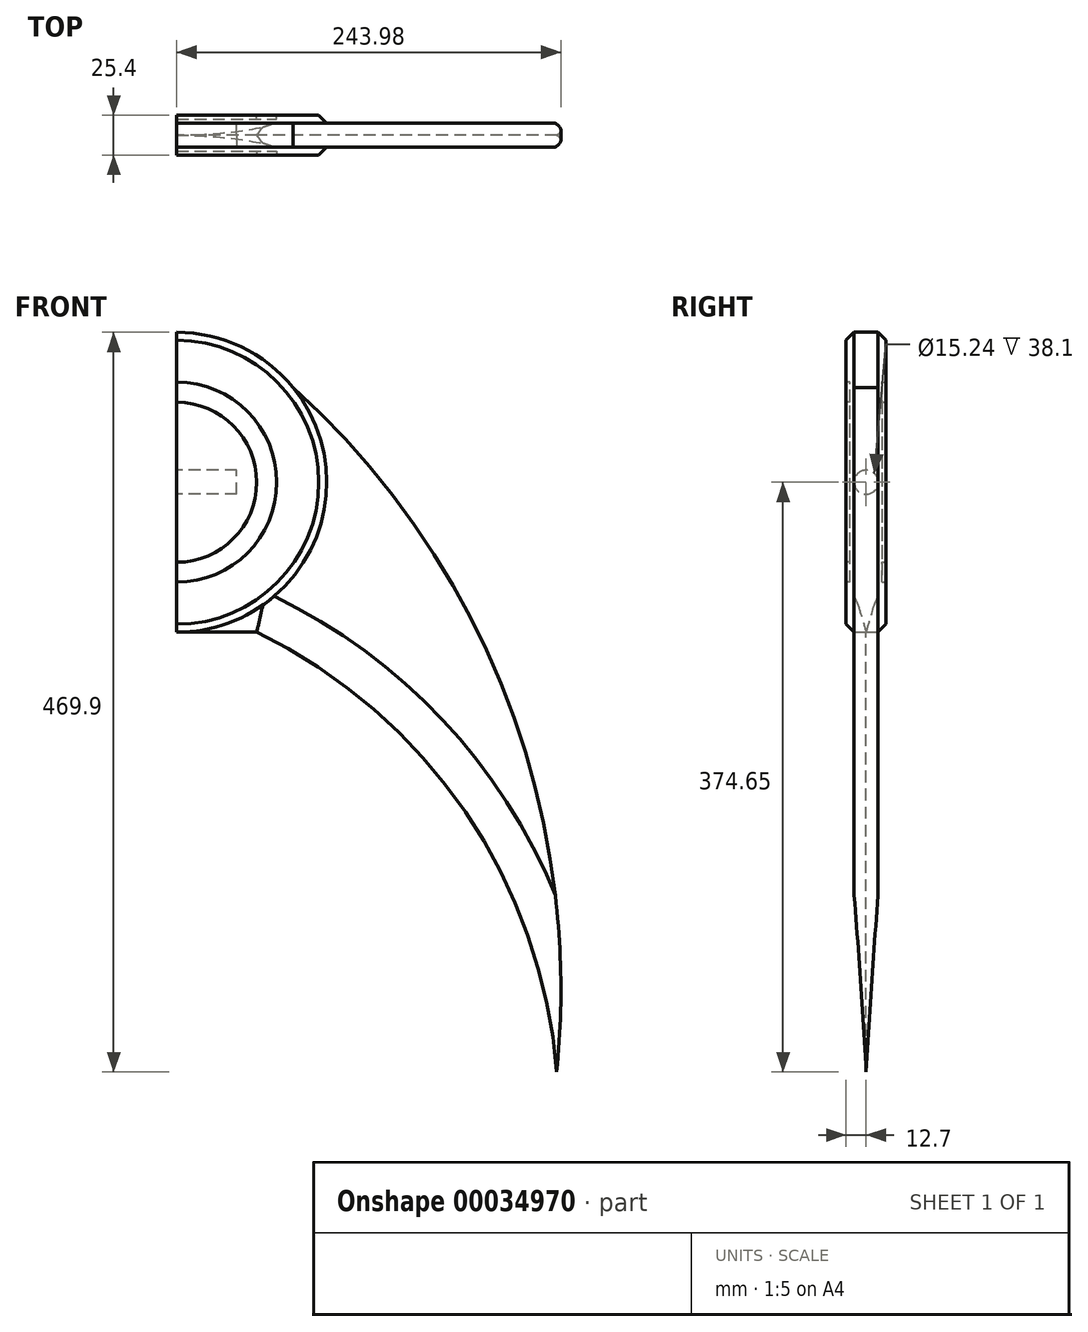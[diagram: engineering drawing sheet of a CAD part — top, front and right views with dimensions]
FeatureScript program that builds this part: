
annotation { "Feature Type Name" : "Feature", "Feature Type Description" : "" }
export const myFeature = defineFeature(function(context is Context, id is Id, definition is map)
    precondition{}
    {
        {
            var Q0;
            Q0=qCreatedBy(makeId("Right.planeOp"),FACE);
            var sketch = newSketch(context, id + "F0", { "sketchPlane" : qUnion([Q0])});
            skCircle(sketch, "E0", {"center": v(0, 0) * mm, "radius": 7.62 * mm});
            skSolve(sketch);
        }
        {
            var Q0;
            Q0=makeQuery(id+"F0.imprint","IMPRINT",FACE,{"disambiguationData":[TD([[makeQuery(id+"F0.imprint","IMPRINT",EDGE,{"derivedFrom":sQuery(id+"F0.wireOp",EDGE,"E0")}),1.0]])]});
            extrude(context, id + "F1", {"entities" : qUnion([Q0]), "depth" : 38.1 * mm});
        }
        {
            var Q0;
            Q0=qCreatedBy(makeId("Front.planeOp"),FACE);
            var sketch = newSketch(context, id + "F2", { "sketchPlane" : qUnion([Q0])});
            skLineSegment(sketch, "E1.0", {"start": v(38.1, 7.62) * mm, "end": v(38.1, -7.62) * mm});
            skArc(sketch, "E2", {"start": v(111.98, 60.11) * mm, "mid": v(79, 86.02) * mm, "end": v(38.1, 95.25) * mm});
            skLineSegment(sketch, "E3", {"start": v(38.1, 0) * mm, "end": v(38.1, 95.25) * mm});
            skLineSegment(sketch, "E4", {"start": v(38.1, 0) * mm, "end": v(38.1, -95.25) * mm});
            skLineSegment(sketch, "E5", {"start": v(38.1, -95.25) * mm, "end": v(88.9, -95.25) * mm});
            skArc(sketch, "E6", {"start": v(279.4, -374.65) * mm, "mid": v(221.44, -209.52) * mm, "end": v(88.9, -95.25) * mm});
            skArc(sketch, "E7", {"start": v(279.4, -374.65) * mm, "mid": v(247.68, -137.25) * mm, "end": v(111.98, 60.11) * mm});
            skSolve(sketch);
        }
        {
            var Q0;
            {var subQ3=sQuery(id+"F2.wireOp",EDGE,"E2");Q0=makeQuery(id+"F2.imprint","IMPRINT",FACE,{"disambiguationData":[TD([[makeQuery(id+"F2.imprint","IMPRINT",EDGE,{"derivedFrom":subQ3}),1.0]])]});}
            extrude(context, id + "F3", {"entities" : qUnion([Q0]), "operationType" : NewBodyOperationType.ADD, "endBound" : BoundingType.SYMMETRIC, "depth" : 15.24 * mm});
        }
        {
            var Q0;
            Q0=makeQuery(id+"F3.opExtrude","CAP_EDGE",EDGE,{"disambiguationData":[OSD([sQuery(id+"F2.wireOp",EDGE,"E6")])],"isStart":false});
            var Q1;
            Q1=makeQuery(id+"F3.opExtrude","CAP_EDGE",EDGE,{"disambiguationData":[OSD([sQuery(id+"F2.wireOp",EDGE,"E5")])],"isStart":false});
            chamfer(context, id + "F4", {"entities" : qUnion([Q0, Q1]), "chamferType" : ChamferType.TWO_OFFSETS, "width1" : 7.62 * mm, "oppositeDirection" : false, "width2" : 25.4 * mm, "tangentPropagation" : true});
        }
        {
            var Q0;
            Q0=makeQuery(id+"F3.opExtrude","CAP_EDGE",EDGE,{"disambiguationData":[OSD([sQuery(id+"F2.wireOp",EDGE,"E6")])],"isStart":true});
            var Q1;
            Q1=makeQuery(id+"F3.opExtrude","CAP_EDGE",EDGE,{"disambiguationData":[OSD([sQuery(id+"F2.wireOp",EDGE,"E5")])],"isStart":true});
            chamfer(context, id + "F5", {"entities" : qUnion([Q0, Q1]), "chamferType" : ChamferType.TWO_OFFSETS, "width1" : 25.4 * mm, "oppositeDirection" : false, "width2" : 7.62 * mm, "tangentPropagation" : true});
        }
        {
            var Q0;
            Q0=qCreatedBy(makeId("Front.planeOp"),FACE);
            var sketch = newSketch(context, id + "F6", { "sketchPlane" : qUnion([Q0])});
            skLineSegment(sketch, "E8.0", {"start": v(38.1, 0) * mm, "end": v(38.1, 95.25) * mm});
            skCircle(sketch, "E9", {"center": v(38.1, 0) * mm, "radius": 95.25 * mm});
            skLineSegment(sketch, "E10", {"start": v(38.1, 0) * mm, "end": v(38.1, -95.25) * mm});
            skSolve(sketch);
        }
        {
            var Q0;
            {var subQ2=sQuery(id+"F6.wireOp",EDGE,"E8.0");Q0=makeQuery(id+"F6.imprint","IMPRINT",FACE,{"disambiguationData":[TD([[makeQuery(id+"F6.imprint","IMPRINT",EDGE,{"derivedFrom":subQ2}),-1.0]])]});}
            extrude(context, id + "F7", {"entities" : qUnion([Q0]), "operationType" : NewBodyOperationType.ADD, "endBound" : BoundingType.SYMMETRIC, "depth" : 25.4 * mm});
        }
        {
            var Q0;
            Q0=makeQuery(id+"F7.opExtrude","CAP_EDGE",EDGE,{"disambiguationData":[OSD([sQuery(id+"F6.wireOp",EDGE,"E9")])],"isStart":false});
            var Q1;
            Q1=makeQuery(id+"F7.opExtrude","CAP_EDGE",EDGE,{"disambiguationData":[OSD([sQuery(id+"F6.wireOp",EDGE,"E9")])],"isStart":true});
            chamfer(context, id + "F8", {"entities" : qUnion([Q0, Q1]), "width" : 5.08 * mm, "tangentPropagation" : true});
        }
        {
            var Q0;
            Q0=makeQuery(id+"F7.opExtrude","CAP_FACE",FACE,{"disambiguationData":[OSD([sQuery(id+"F6.wireOp",EDGE,"E8.0"),sQuery(id+"F6.wireOp",EDGE,"E9"),sQuery(id+"F6.wireOp",EDGE,"E10")])],"isStart":false});
            var sketch = newSketch(context, id + "F9", { "sketchPlane" : qUnion([Q0])});
            skCircle(sketch, "E11", {"center": v(38.1, 0) * mm, "radius": 63.5 * mm});
            skCircle(sketch, "E12", {"center": v(38.1, 0) * mm, "radius": 50.8 * mm});
            skSolve(sketch);
        }
        {
            var Q0;
            {var subQ0=makeQuery(id+"F7.opExtrude","CAP_EDGE",EDGE,{"disambiguationData":[OSD([sQuery(id+"F6.wireOp",EDGE,"E8.0"),sQuery(id+"F6.wireOp",EDGE,"E10")])],"isStart":false});var subQ3=sQuery(id+"F9.wireOp",EDGE,"E11");var subQ6=makeQuery(id+"F9.imprint","INTERSECT",VERTEX,{"disambiguationData":[OD(0.0)],"derivedFrom":[subQ0,subQ3]});Q0=makeQuery(id+"F9.imprint","IMPRINT",FACE,{"disambiguationData":[TD([[makeQuery(id+"F9.imprint","IMPRINT",EDGE,{"disambiguationData":[TD([[subQ6,1.0]])],"derivedFrom":subQ3}),1.0]])]});}
            extrude(context, id + "F10", {"entities" : qUnion([Q0]), "operationType" : NewBodyOperationType.REMOVE, "oppositeDirection" : true, "depth" : 2.54 * mm});
        }
        {
            var Q0;
            Q0=makeQuery(id+"F7.opExtrude","CAP_FACE",FACE,{"disambiguationData":[OSD([sQuery(id+"F6.wireOp",EDGE,"E8.0"),sQuery(id+"F6.wireOp",EDGE,"E9"),sQuery(id+"F6.wireOp",EDGE,"E10")])],"isStart":true});
            var sketch = newSketch(context, id + "F11", { "sketchPlane" : qUnion([Q0])});
            skCircle(sketch, "E13", {"center": v(-38.1, 0) * mm, "radius": 63.5 * mm});
            skCircle(sketch, "E14", {"center": v(-38.1, 0) * mm, "radius": 50.8 * mm});
            skSolve(sketch);
        }
        {
            var Q0;
            {var subQ0=makeQuery(id+"F7.opExtrude","CAP_EDGE",EDGE,{"disambiguationData":[OSD([sQuery(id+"F6.wireOp",EDGE,"E8.0"),sQuery(id+"F6.wireOp",EDGE,"E10")])],"isStart":true});var subQ3=sQuery(id+"F11.wireOp",EDGE,"E13");var subQ6=makeQuery(id+"F11.imprint","INTERSECT",VERTEX,{"disambiguationData":[OD(0.0)],"derivedFrom":[subQ0,subQ3]});Q0=makeQuery(id+"F11.imprint","IMPRINT",FACE,{"disambiguationData":[TD([[makeQuery(id+"F11.imprint","IMPRINT",EDGE,{"disambiguationData":[TD([[subQ6,-1.0]])],"derivedFrom":subQ3}),1.0]])]});}
            extrude(context, id + "F12", {"entities" : qUnion([Q0]), "operationType" : NewBodyOperationType.REMOVE, "oppositeDirection" : true, "depth" : 2.54 * mm});
        }
        {
            var Q0;
            Q0=makeQuery(id+"F1.opExtrude","CAP_FACE",FACE,{"disambiguationData":[OSD([sQuery(id+"F0.wireOp",EDGE,"E0")])],"isStart":true});
            var sketch = newSketch(context, id + "F13", { "sketchPlane" : qUnion([Q0])});
            skSolve(sketch);
        }
        {
            var Q0;
            Q0=qSketchRegion(id+"F13",true);
            var Q1;
            Q1=makeQuery(id+"F13.imprint","IMPRINT",FACE,{"disambiguationData":[TD([[makeQuery(id+"F13.imprint","IMPRINT",EDGE,{"derivedFrom":makeQuery(id+"F1.opExtrude","CAP_EDGE",EDGE,{"disambiguationData":[OSD([sQuery(id+"F0.wireOp",EDGE,"E0")])],"isStart":true})}),-1.0]])]});
            extrude(context, id + "F14", {"entities" : qUnion([Q0, Q1]), "operationType" : NewBodyOperationType.REMOVE, "oppositeDirection" : true, "depth" : 76.2 * mm});
        }
    });
